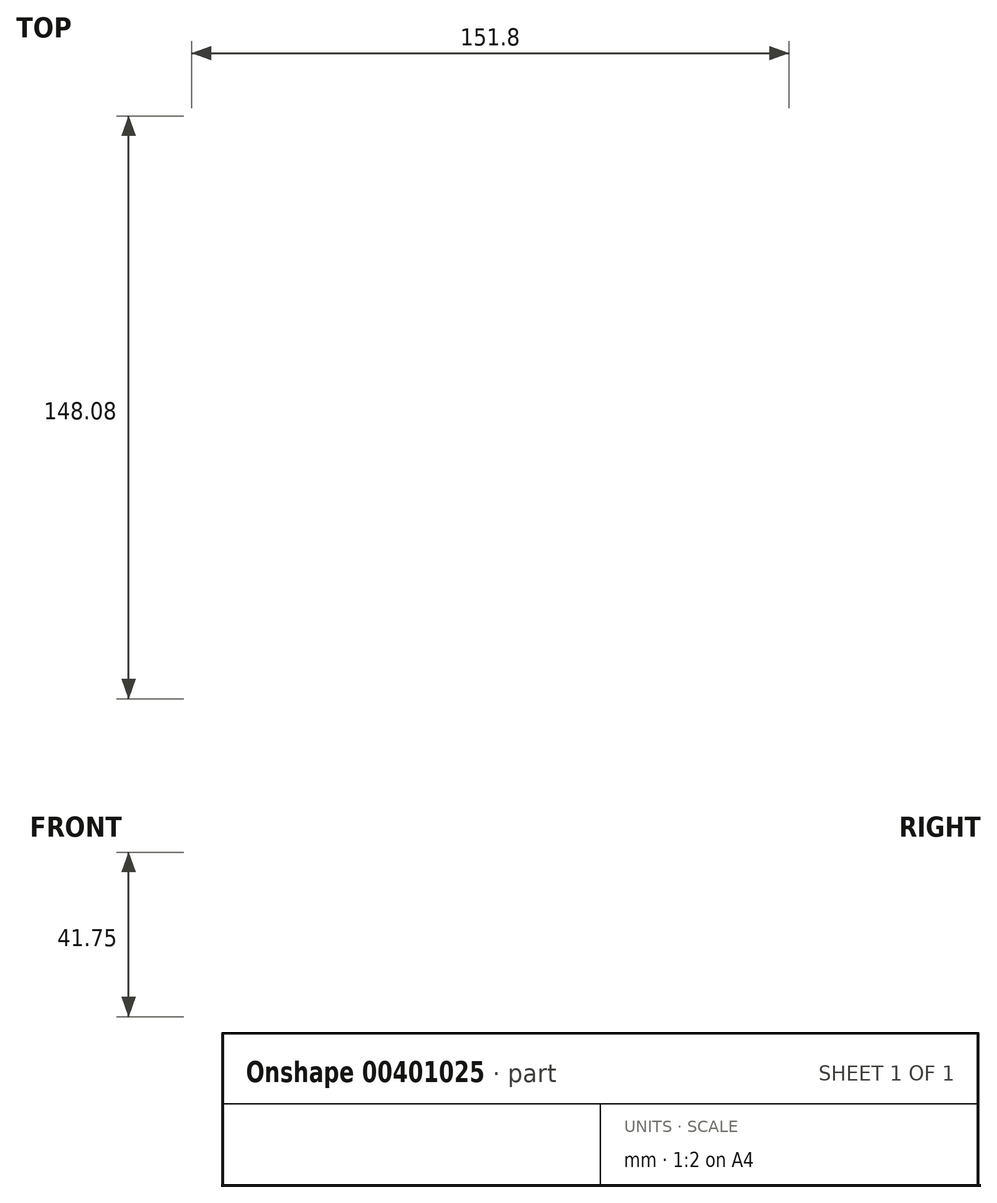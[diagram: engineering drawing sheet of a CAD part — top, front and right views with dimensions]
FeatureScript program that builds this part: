
annotation { "Feature Type Name" : "Feature", "Feature Type Description" : "" }
export const myFeature = defineFeature(function(context is Context, id is Id, definition is map)
    precondition{}
    {
        {
            var Q0;
            Q0=qCreatedBy(makeId("Top.planeOp"),FACE);
            cPlane(context, id + "F0", {"entities" : qUnion([Q0]), "cplaneType" : CPlaneType.OFFSET, "offset" : 39.88 * mm, "width" : 152.4 * mm, "height" : 152.4 * mm});
        }
        {
            var Q0;
            Q0=qCreatedBy(id+"F0.planeOp",FACE);
            var sketch = newSketch(context, id + "F1", { "sketchPlane" : qUnion([Q0])});
            skCircle(sketch, "E0", {"center": v(-65.51, 62.2) * mm, "radius": 28.85 * mm});
            skSolve(sketch);
        }
        {
            var Q0;
            Q0=qCreatedBy(makeId("Top.planeOp"),FACE);
            var sketch = newSketch(context, id + "F2", { "sketchPlane" : qUnion([Q0])});
            skFitSpline(sketch, "E1", {"points": [v(-62.47, -52.99) * mm, v(-61.14, 0) * mm, v(9.5, 19.58) * mm, v(56.3, -40.11) * mm, v(10, -52.74) * mm, v(-17.97, -19.54) * mm, v(-62.47, -52.99) * mm]});
            skSolve(sketch);
        }
        {
            var Q0;
            Q0=makeQuery(id+"F2.imprint","IMPRINT",FACE,{"disambiguationData":[TD([[makeQuery(id+"F2.imprint","IMPRINT",EDGE,{"derivedFrom":sQuery(id+"F2.wireOp",EDGE,"E1")}),-1.0]])]});
            var Q1;
            Q1=makeQuery(id+"F1.imprint","IMPRINT",FACE,{"disambiguationData":[TD([[makeQuery(id+"F1.imprint","IMPRINT",EDGE,{"derivedFrom":sQuery(id+"F1.wireOp",EDGE,"E0")}),1.0]])]});
            loft(context, id + "F3", {"sheetProfilesArray" : [{ "sheetProfileEntities" : qUnion([Q0]) }, { "sheetProfileEntities" : qUnion([Q1]) }]});
        }
        {
            var Q0;
            Q0=makeQuery(id+"F3.opLoft","CAP_FACE",FACE,{"disambiguationData":[OSD([makeQuery(id+"F1.imprint","IMPRINT",FACE,{"disambiguationData":[TD([[makeQuery(id+"F1.imprint","IMPRINT",EDGE,{"derivedFrom":sQuery(id+"F1.wireOp",EDGE,"E0")}),1.0]])]})])],"isStart":true});
            shell(context, id + "F4", {"entities" : qUnion([Q0]), "thickness" : 2.54 * mm});
        }
    });
